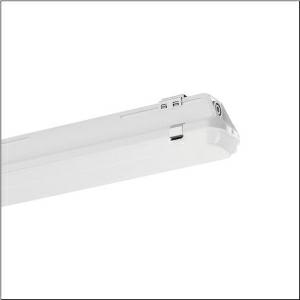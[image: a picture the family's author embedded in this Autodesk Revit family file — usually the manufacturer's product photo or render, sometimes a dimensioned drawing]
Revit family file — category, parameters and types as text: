
# Revit family: monsun_r__11_51fp10ep460l007_54c8
name_source: partatom
category: Lighting Fixtures
units: mm (PartAtom-declared; Revit-internal decimal feet)

## family parameters
Cut with Voids When Loaded = No
Host = Face
Light Source = No
Part Type = Normal
Room Calculation Point = No
Round Connector Dimension = Use Diameter
Shared = No

## types (1)
- --- (1 x LED, 6050 lm, 31.5 W, 4000K)
    Apparent Load = 32 VA
    CIE Flux Codes = 47 77 93 94 100
    Color Rendering = 80
    Color Temperature = 4000K
    Default Elevation = 1800 mm
    Description = Monsun® 11, damp-proof luminaire, chain hanger, primary optical cover: enclosure, of PMMA, light emission: direct distribution, primary light characteristic: symmetric, installation type: suspended mounting, surface-mounted, horizontal mounting, vertical mounting, LED, rated luminous flux: 6.050lm, luminous efficacy: 192lm/W, light colour: 840, colour temperature: 4000K, control gear: DALI 2, with terminal, 5-pole, max. 2.5mm², through-wiring: 7x 2.5mm², mains connection: 220..240V, AC, 50/60Hz, rated input power: 32W, housing, of glass-fibre reinforced polyester, uncoated, bright grey, incl. chain hanger, length: 1.590mm, width: 90mm, height: 88mm, clip for enclosure, of stainless steel (V2A), ceiling mounting element, of stainless steel (V2A), chain hanger, of stainless steel (V2A), protection rating (complete): IP66, insulation class (complete): insulation class I (protective earthing), certification: CE, ENEC, VDE, UKCA, protection symbol: D, impact resistance: IK04, permissible operating ambient temperature: -25..+40°C, standard: EN 50419, EN 60598-2-1, corresponds to IFS (International Featured Standards) requirements for safety and quality in the food industry, for indoor or canopied outdoor use, no direct snow, no direct sun, no direct rain, LABS conformity tested according to VDMA 24364:2018-05, contact your sales advisor before using the luminaires in applications with unclear chemical exposure, large temperature fluctuations or condensation-forming humidity, packaging unit: 1 piece
    Height = 89 mm
    Lamp = 1 x LED
    Lamp Light Flux = 6050 lm
    Lamp Power = 31.5 W
    Lamp count = 1
    Length = 1590 mm
    Luminous efficacy = 192 lm/W
    Manufacturer = Siteco
    ModVariant = No
    Model = 51FP10EP460L007
    Mounting Place = Ceiling
    Mounting Type = Surface mounted
    Number of Poles = 1
    OnlyDefault = Yes
    Power Factor = 1
    Product Name = Monsun® 11
    Product group = damp-proof luminaire
    ProductGroupID = 300
    Protection Class = Protection class I
    Protection Degree = IP 66
    RLX_Detail_Level = 1
    RLX_Emergency_Light_Flux = 0 lm
    RLX_Emergency_Type = 0
    RLX_Emergency_Type_DB = No
    RlxData = <blob elided: 92261 chars, md5=a8099262>
    Socket = socket
    Standby Power = 0 W
    System Light Flux = 6050 lm
    System Power = 32 W
    Type Comments = factory setting: luminous flux: 100 % | dim-lin: 254 | 219 mA
    Type Image = l_1349237.jpg
    URL = http://relux.com
    VarID = @adj_017754
    Voltage = 0 V
    Weight = 0.00 kg
    Width = 90 mm

## geometry (parser evidence)
native form markers: Blend x4, Sweep x12
no freeform markers — native parametric forms only
